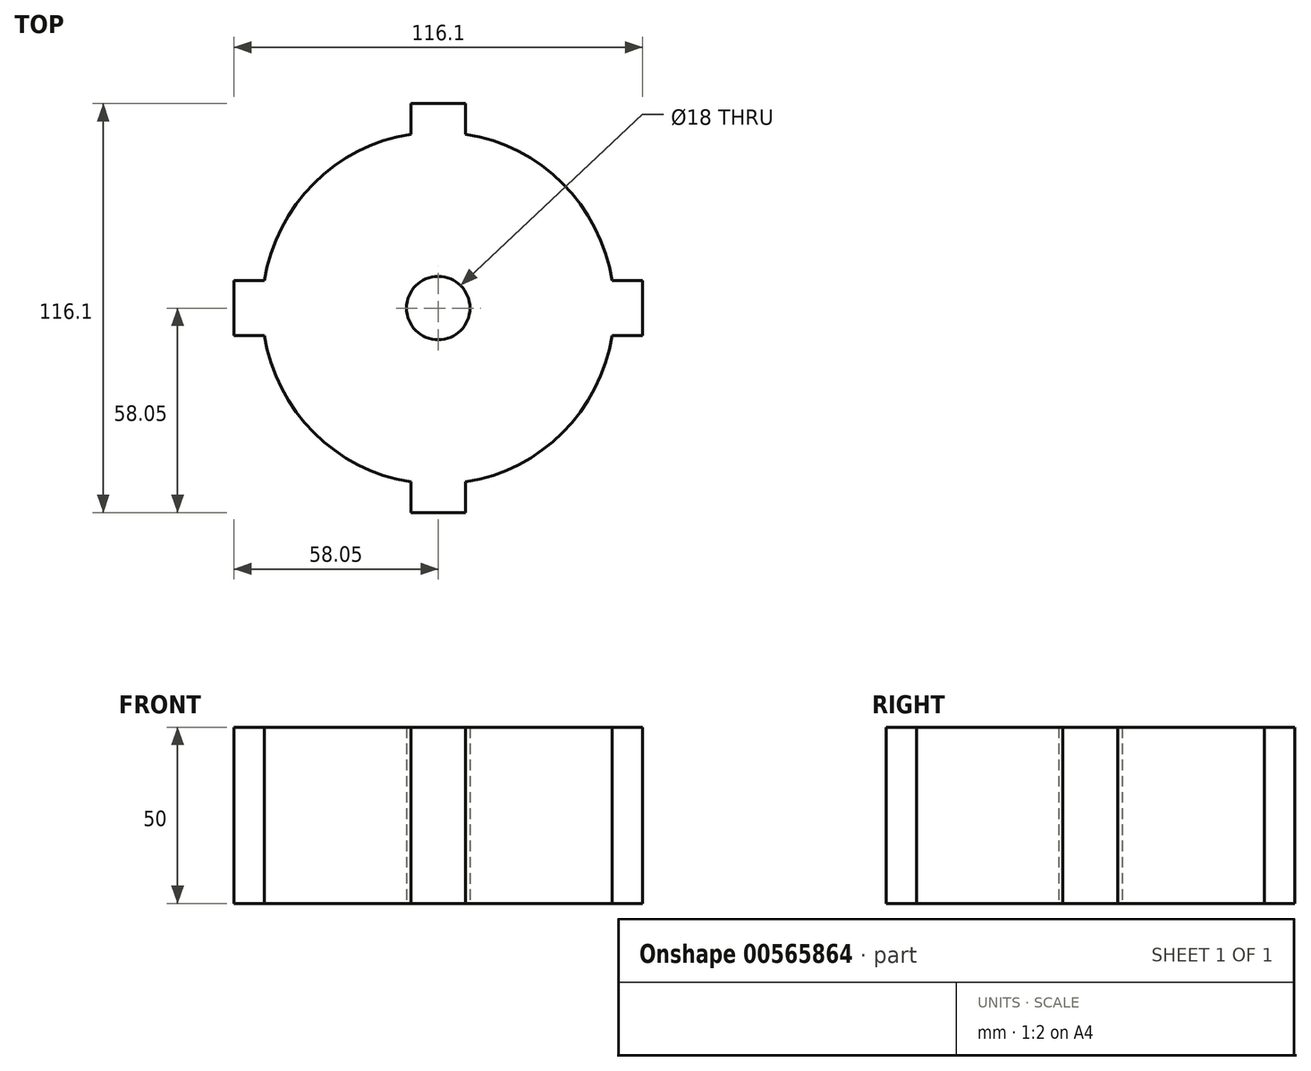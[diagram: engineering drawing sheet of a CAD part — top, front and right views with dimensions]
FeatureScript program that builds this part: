
annotation { "Feature Type Name" : "Feature", "Feature Type Description" : "" }
export const myFeature = defineFeature(function(context is Context, id is Id, definition is map)
    precondition{}
    {
        {
            var Q0;
            Q0=qCreatedBy(makeId("Top.planeOp"),FACE);
            var sketch = newSketch(context, id + "F0", { "sketchPlane" : qUnion([Q0])});
            skCircle(sketch, "E0", {"center": v(0, 0) * mm, "radius": 50 * mm});
            skCircle(sketch, "E1", {"center": v(0, 0) * mm, "radius": 9 * mm});
            skLineSegment(sketch, "E2", {"start": v(-7.8, 49.39) * mm, "end": v(-7.8, 58.05) * mm});
            skLineSegment(sketch, "E3", {"start": v(-7.8, 58.05) * mm, "end": v(7.8, 58.05) * mm});
            skLineSegment(sketch, "E4", {"start": v(7.8, 58.05) * mm, "end": v(7.8, 49.39) * mm});
            skLineSegment(sketch, "E5", {"start": v(49.39, 7.8) * mm, "end": v(58.05, 7.8) * mm});
            skLineSegment(sketch, "E6", {"start": v(58.05, 7.8) * mm, "end": v(58.05, -7.8) * mm});
            skLineSegment(sketch, "E7", {"start": v(58.05, -7.8) * mm, "end": v(49.39, -7.8) * mm});
            skLineSegment(sketch, "E8", {"start": v(7.8, -49.39) * mm, "end": v(7.8, -58.05) * mm});
            skLineSegment(sketch, "E9", {"start": v(7.8, -58.05) * mm, "end": v(-7.8, -58.05) * mm});
            skLineSegment(sketch, "E10", {"start": v(-7.8, -58.05) * mm, "end": v(-7.8, -49.39) * mm});
            skLineSegment(sketch, "E11", {"start": v(-49.39, -7.8) * mm, "end": v(-58.05, -7.8) * mm});
            skLineSegment(sketch, "E12", {"start": v(-58.05, -7.8) * mm, "end": v(-58.05, 7.8) * mm});
            skLineSegment(sketch, "E13", {"start": v(-58.05, 7.8) * mm, "end": v(-49.39, 7.8) * mm});
            skSolve(sketch);
        }
        {
            var Q0;
            Q0=makeQuery(id+"F0.imprint","IMPRINT",FACE,{"disambiguationData":[TD([[makeQuery(id+"F0.imprint","IMPRINT",EDGE,{"derivedFrom":sQuery(id+"F0.wireOp",EDGE,"E0")}),1.0]])]});
            var Q1;
            {var subQ0=sQuery(id+"F0.wireOp",EDGE,"E2");Q1=makeQuery(id+"F0.imprint","IMPRINT",FACE,{"disambiguationData":[TD([[makeQuery(id+"F0.imprint","IMPRINT",EDGE,{"derivedFrom":subQ0}),-1.0]])]});}
            var Q2;
            {var subQ0=sQuery(id+"F0.wireOp",EDGE,"E5");Q2=makeQuery(id+"F0.imprint","IMPRINT",FACE,{"disambiguationData":[TD([[makeQuery(id+"F0.imprint","IMPRINT",EDGE,{"derivedFrom":subQ0}),-1.0]])]});}
            var Q3;
            {var subQ0=sQuery(id+"F0.wireOp",EDGE,"E8");Q3=makeQuery(id+"F0.imprint","IMPRINT",FACE,{"disambiguationData":[TD([[makeQuery(id+"F0.imprint","IMPRINT",EDGE,{"derivedFrom":subQ0}),-1.0]])]});}
            var Q4;
            {var subQ0=sQuery(id+"F0.wireOp",EDGE,"E11");Q4=makeQuery(id+"F0.imprint","IMPRINT",FACE,{"disambiguationData":[TD([[makeQuery(id+"F0.imprint","IMPRINT",EDGE,{"derivedFrom":subQ0}),-1.0]])]});}
            extrude(context, id + "F1", {"entities" : qUnion([Q0, Q1, Q2, Q3, Q4]), "depth" : 50 * mm, "offsetDistance" : 25 * mm});
        }
    });
